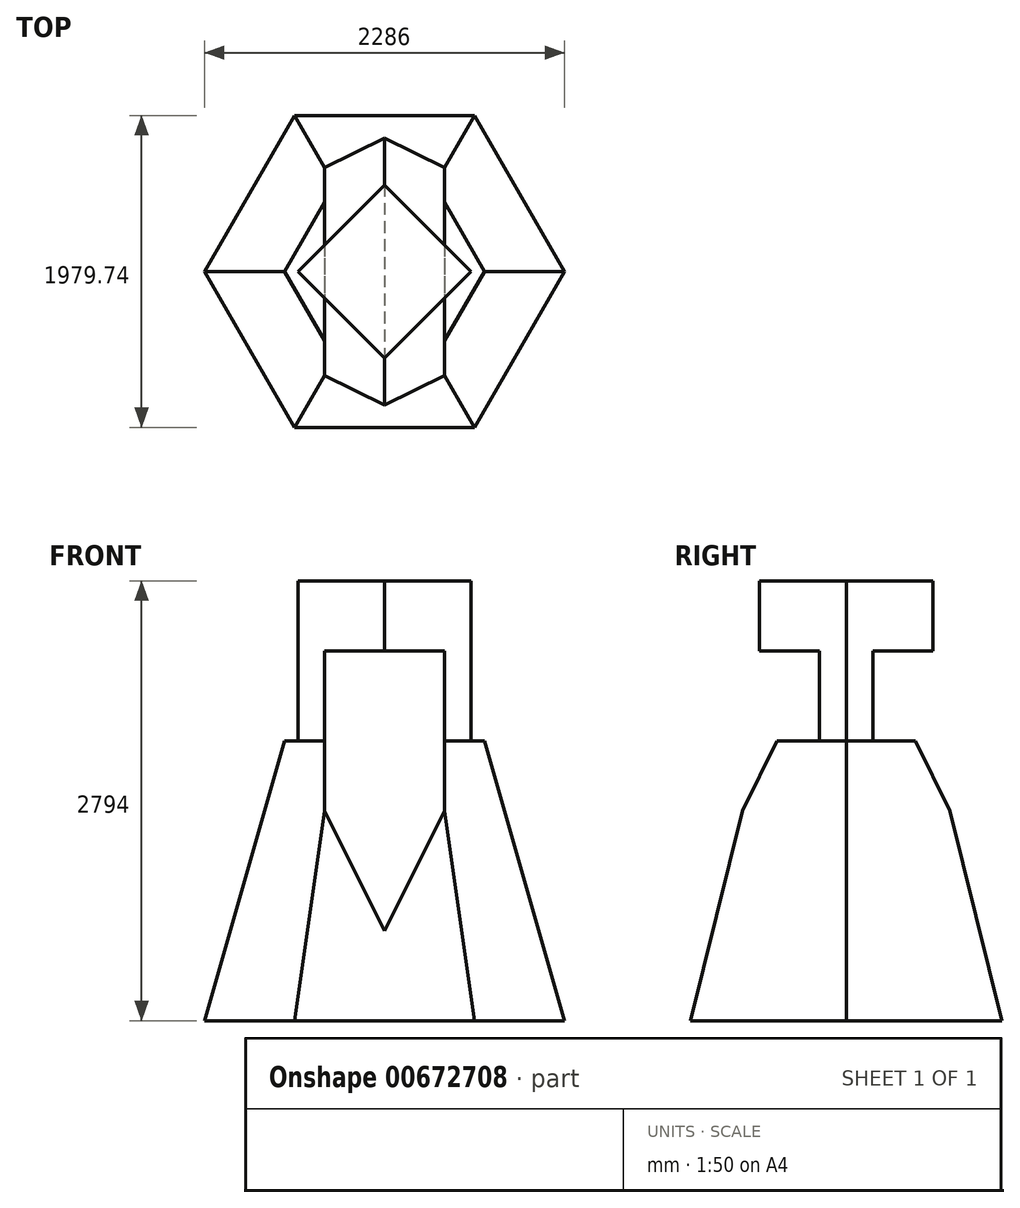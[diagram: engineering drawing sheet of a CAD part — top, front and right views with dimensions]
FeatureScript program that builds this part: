
annotation { "Feature Type Name" : "Feature", "Feature Type Description" : "" }
export const myFeature = defineFeature(function(context is Context, id is Id, definition is map)
    precondition{}
    {
        {
            var Q0;
            Q0=qCreatedBy(makeId("Top.planeOp"),FACE);
            var sketch = newSketch(context, id + "F0", { "sketchPlane" : qUnion([Q0])});
            skCircle(sketch, "E0.cCircle", {"center": v(0, 0) * mm, "radius": 1143 * mm, "construction": true});
            skLineSegment(sketch, "E0.0", {"start": v(-1143, 0) * mm, "end": v(-571.5, 989.87) * mm});
            skLineSegment(sketch, "E0.1", {"start": v(-571.5, 989.87) * mm, "end": v(571.5, 989.87) * mm});
            skLineSegment(sketch, "E0.2", {"start": v(571.5, 989.87) * mm, "end": v(1143, 0) * mm});
            skLineSegment(sketch, "E0.3", {"start": v(1143, 0) * mm, "end": v(571.5, -989.87) * mm});
            skLineSegment(sketch, "E0.4", {"start": v(571.5, -989.87) * mm, "end": v(-571.5, -989.87) * mm});
            skLineSegment(sketch, "E0.5", {"start": v(-571.5, -989.87) * mm, "end": v(-1143, 0) * mm});
            skSolve(sketch);
        }
        {
            var Q0;
            Q0=qCreatedBy(makeId("Top.planeOp"),FACE);
            cPlane(context, id + "F1", {"entities" : qUnion([Q0]), "cplaneType" : CPlaneType.OFFSET, "offset" : 1778 * mm, "width" : 152.4 * mm, "height" : 152.4 * mm});
        }
        {
            var Q0;
            Q0=qCreatedBy(id+"F1.planeOp",FACE);
            var sketch = newSketch(context, id + "F2", { "sketchPlane" : qUnion([Q0])});
            skCircle(sketch, "E1.cCircle", {"center": v(0, 0) * mm, "radius": 635 * mm, "construction": true});
            skLineSegment(sketch, "E1.0", {"start": v(635, 0) * mm, "end": v(317.5, -549.93) * mm});
            skLineSegment(sketch, "E1.1", {"start": v(317.5, -549.93) * mm, "end": v(-317.5, -549.93) * mm});
            skLineSegment(sketch, "E1.2", {"start": v(-317.5, -549.93) * mm, "end": v(-635, 0) * mm});
            skLineSegment(sketch, "E1.3", {"start": v(-635, 0) * mm, "end": v(-317.5, 549.93) * mm});
            skLineSegment(sketch, "E1.4", {"start": v(-317.5, 549.93) * mm, "end": v(317.5, 549.93) * mm});
            skLineSegment(sketch, "E1.5", {"start": v(317.5, 549.93) * mm, "end": v(635, 0) * mm});
            skSolve(sketch);
        }
        {
            var Q0;
            Q0=makeQuery(id+"F0.imprint","IMPRINT",FACE,{"disambiguationData":[TD([[makeQuery(id+"F0.imprint","IMPRINT",EDGE,{"derivedFrom":sQuery(id+"F0.wireOp",EDGE,"E0.0")}),-1.0]])]});
            var Q1;
            Q1=makeQuery(id+"F2.imprint","IMPRINT",FACE,{"disambiguationData":[TD([[makeQuery(id+"F2.imprint","IMPRINT",EDGE,{"derivedFrom":sQuery(id+"F2.wireOp",EDGE,"E1.0")}),-1.0]])]});
            loft(context, id + "F3", {"sheetProfilesArray" : [{ "sheetProfileEntities" : qUnion([Q0]) }, { "sheetProfileEntities" : qUnion([Q1]) }]});
        }
        {
            var Q0;
            Q0=makeQuery(id+"F3.opLoft","CAP_FACE",FACE,{"disambiguationData":[OSD([makeQuery(id+"F2.imprint","IMPRINT",FACE,{"disambiguationData":[TD([[makeQuery(id+"F2.imprint","IMPRINT",EDGE,{"derivedFrom":sQuery(id+"F2.wireOp",EDGE,"E1.0")}),-1.0]])]})])],"isStart":true});
            var sketch = newSketch(context, id + "F4", { "sketchPlane" : qUnion([Q0])});
            skCircle(sketch, "E2.cCircle", {"center": v(0, 0) * mm, "radius": 549.93 * mm, "construction": true});
            skLineSegment(sketch, "E2.0", {"start": v(549.93, 0) * mm, "end": v(0, -549.93) * mm});
            skLineSegment(sketch, "E2.1", {"start": v(0, -549.93) * mm, "end": v(-549.93, 0) * mm});
            skLineSegment(sketch, "E2.2", {"start": v(-549.93, 0) * mm, "end": v(0, 549.93) * mm});
            skLineSegment(sketch, "E2.3", {"start": v(0, 549.93) * mm, "end": v(549.93, 0) * mm});
            skSolve(sketch);
        }
        {
            var Q0;
            Q0=makeQuery(id+"F4.imprint","IMPRINT",FACE,{"disambiguationData":[TD([[makeQuery(id+"F4.imprint","IMPRINT",EDGE,{"derivedFrom":sQuery(id+"F4.wireOp",EDGE,"E2.0")}),-1.0]])]});
            extrude(context, id + "F5", {"entities" : qUnion([Q0]), "operationType" : NewBodyOperationType.ADD, "depth" : 1016 * mm, "offsetDistance" : 25.4 * mm});
        }
        {
            var Q0;
            Q0=qCreatedBy(makeId("Front.planeOp"),FACE);
            var sketch = newSketch(context, id + "F6", { "sketchPlane" : qUnion([Q0])});
            skLineSegment(sketch, "E3", {"start": v(-381, 1333.5) * mm, "end": v(-381, 2349.5) * mm});
            skLineSegment(sketch, "E4", {"start": v(-381, 2349.5) * mm, "end": v(381, 2349.5) * mm});
            skLineSegment(sketch, "E5", {"start": v(381, 2349.5) * mm, "end": v(381, 1333.5) * mm});
            skLineSegment(sketch, "E6", {"start": v(381, 1333.5) * mm, "end": v(0, 571.5) * mm});
            skLineSegment(sketch, "E7", {"start": v(0, 571.5) * mm, "end": v(-381, 1333.5) * mm});
            skPoint(sketch, "E8.orphan", {"position": v(-317.5, 1778) * mm});
            skPoint(sketch, "E9.orphan", {"position": v(317.5, 1778) * mm});
            skPoint(sketch, "E10.0.start.orphan", {"position": v(571.5, 0) * mm});
            skPoint(sketch, "E11.0.start.orphan", {"position": v(-571.5, 0) * mm});
            skSolve(sketch);
        }
        {
            var Q0;
            Q0 = qSketchRegion(id + "F6", true);
            extrude(context, id + "F7", {"entities" : qUnion([Q0]), "operationType" : NewBodyOperationType.REMOVE, "endBound" : BoundingType.SYMMETRIC, "oppositeDirection" : true, "depth" : 2377.44 * mm, "offsetDistance" : 25.4 * mm});
        }
    });
